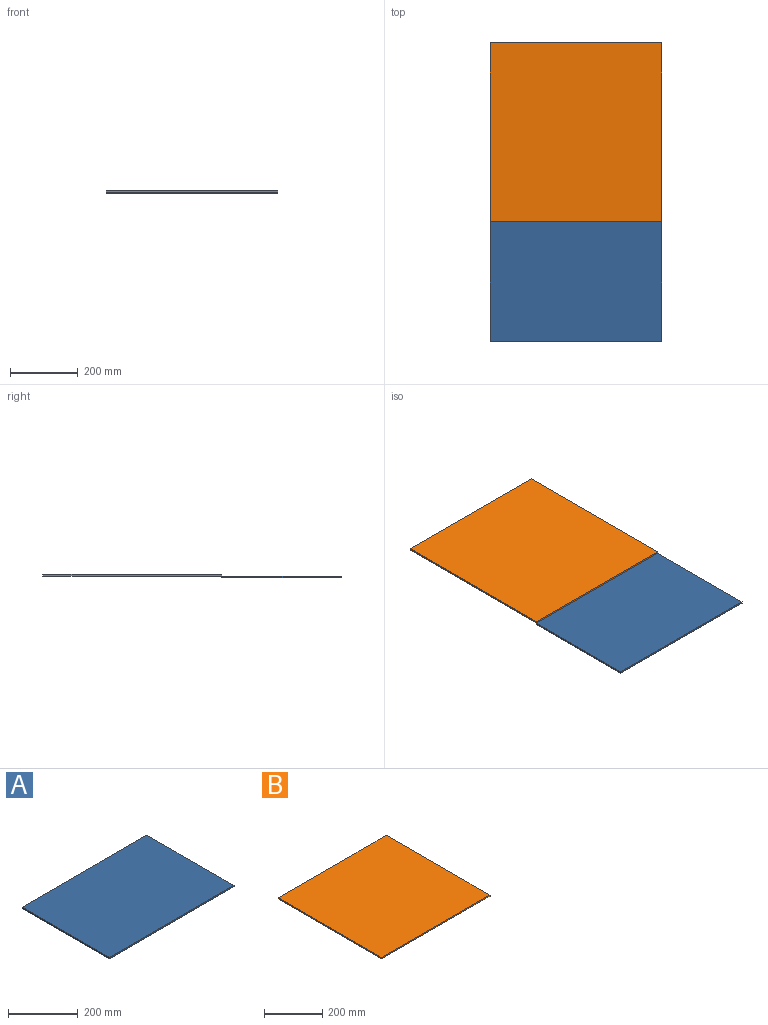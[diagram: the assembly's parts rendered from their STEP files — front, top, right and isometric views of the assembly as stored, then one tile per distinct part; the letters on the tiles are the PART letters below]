
ASSEMBLY  parts=2 mates=1
PART A: 6 faces, bbox 505x352x5 mm
  f0: plane 505x5mm, normal (0,-1,0), area 2525mm2, adj f1,f3,f4,f5
  f1: plane 352x5mm, normal (1,0,0), area 1760mm2, adj f0,f2,f4,f5
  f2: plane 505x5mm, normal (0,1,0), area 2525mm2, adj f1,f3,f4,f5
  f3: plane 352x5mm, normal (-1,0,0), area 1760mm2, adj f0,f2,f4,f5
  f4: plane 505x352mm, normal (0,0,1), area 177760mm2, adj f0,f1,f2,f3
  f5: plane 505x352mm, normal (0,0,-1), area 177760mm2, adj f0,f1,f2,f3
PART B: 6 faces, bbox 528x505x5 mm
  f0: plane 528x5mm, normal (0,-1,0), area 2640mm2, adj f1,f3,f4,f5
  f1: plane 505x5mm, normal (1,0,0), area 2525mm2, adj f0,f2,f4,f5
  f2: plane 528x5mm, normal (0,1,0), area 2640mm2, adj f1,f3,f4,f5
  f3: plane 505x5mm, normal (-1,0,0), area 2525mm2, adj f0,f2,f4,f5
  f4: plane 528x505mm, normal (0,0,1), area 266640mm2, adj f0,f1,f2,f3
  f5: plane 528x505mm, normal (0,0,-1), area 266640mm2, adj f0,f1,f2,f3
PLACE A at identity
PLACE B rot(axis=(-0.71,0.71,0),180deg) t=(0,440,10)mm
MATE fastened B.f4 <-> A.f4  axis (0,0,-1) through (252.5,176,5)mm
